# Revit family: Plumbing-Urinal-Combos-Sloan-Valve-WEUS-12001004_
name_source: partatom
category: Plumbing Fixtures
units: mm (PartAtom-declared; Revit-internal decimal feet)

## family parameters
Cut with Voids When Loaded = No
Host = Face
OmniClass Number = 23.45.05.21.11.21
OmniClass Title = Urinals
Part Type = Normal
Room Calculation Point = No
Round Connector Dimension = Use Diameter
Shared = No

## types (1)
- WEUS-1200.1004
    Assembly Code = D2010
    CW Connection = Yes
    CWFU = 0
    Default Elevation = 0"
    Depth = 14 1/2"
    Description = SU-1200 Urinal and GEM-2 186 Flushometer.
    Edition number = 1
    Flush Rate = 0.125 gpf (0.5 Lpf)
    Flushometer Code = 3072619
    Flushometer Material = Sloan Valve - Finish - Polished Chrome
    HW Connection = Yes
    HWFU = 0
    Height = 25 1/4"
    Keynote = 15410
    Manufacturer = Sloan Valve
    Model = WEUS-1200.1004
    Operating Water Pressure = 15 – 80 PSI (103 – 552 kPa). Specific fixtures may require greater minimum flowing pressure - consult manufacturer requirements.
    Part Number = 12001004
    Product Material = Sloan Valve - Vitreous China - White
    Product data url = https://bimobject.com
    Sanitary Drain Connection Diameter = 2"
    URL = www.sloanvalve.com
    Urinal Code = 1101200
    Valve Pressure Drop = 0.00 psi
    Vent Connection = Yes
    WFU = 5
    Waste Connection = Yes
    Water Inlet Connection Diameter = 1"
    Width = 20 3/4"

## geometry (parser evidence)
native form markers: Sweep x3
no freeform markers — native parametric forms only
